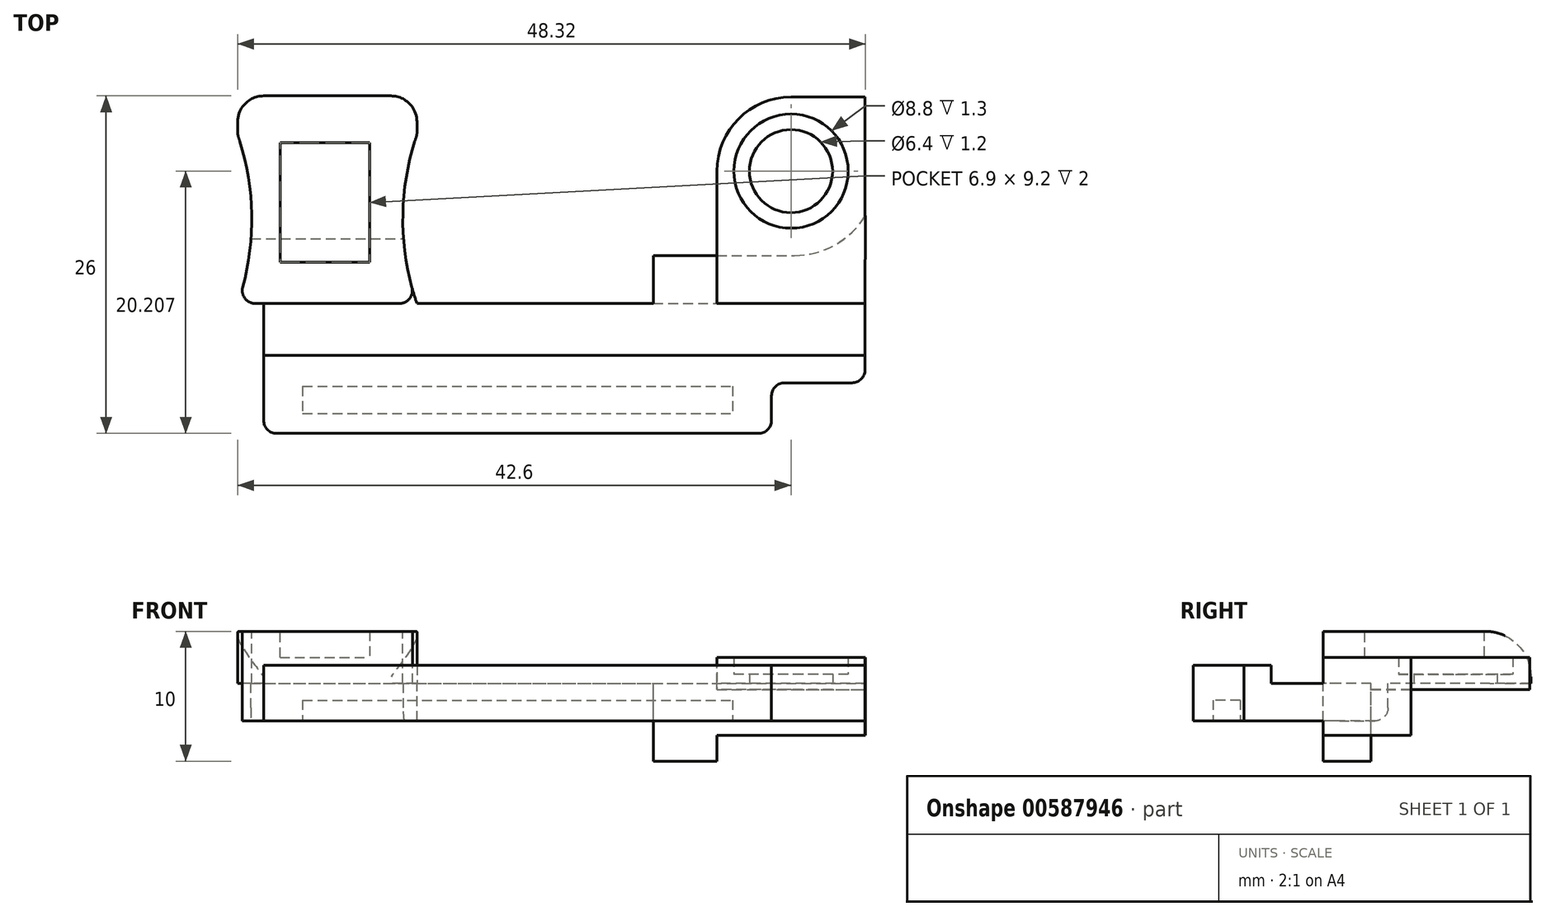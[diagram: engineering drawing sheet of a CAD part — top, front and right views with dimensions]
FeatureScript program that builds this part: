
annotation { "Feature Type Name" : "Feature", "Feature Type Description" : "" }
export const myFeature = defineFeature(function(context is Context, id is Id, definition is map)
    precondition{}
    {
        {
            var Q0;
            Q0=qCreatedBy(makeId("Top.planeOp"),FACE);
            var sketch = newSketch(context, id + "F0", { "sketchPlane" : qUnion([Q0])});
            skLineSegment(sketch, "E0.bottom", {"start": v(32.3, 6) * mm, "end": v(78.6, 6) * mm});
            skLineSegment(sketch, "E0.top", {"start": v(32.3, 0) * mm, "end": v(71.4, 0) * mm});
            skLineSegment(sketch, "E0.left", {"start": v(32.3, 6) * mm, "end": v(32.3, 0) * mm});
            skLineSegment(sketch, "E0.right", {"start": v(78.6, 6) * mm, "end": v(78.6, 3.9) * mm});
            skLineSegment(sketch, "E1.right", {"start": v(71.4, 0) * mm, "end": v(71.4, 3.9) * mm});
            skFitSpline(sketch, "E2", {"points": [v(32.3, 6) * mm, v(78.6, 6) * mm], "startDerivative": vector(78.6, 0) * mm, "endDerivative": vector(78.6, 0) * mm});
            skLineSegment(sketch, "E3", {"start": v(71.4, 3.9) * mm, "end": v(78.6, 3.9) * mm});
            skPoint(sketch, "E4.orphan", {"position": v(78.6, 0) * mm});
            skSolve(sketch);
        }
        {
            var Q0;
            {var subQ3=sQuery(id+"F0.wireOp",EDGE,"E0.left");Q0=makeQuery(id+"F0.imprint","IMPRINT",FACE,{"disambiguationData":[TD([[makeQuery(id+"F0.imprint","IMPRINT",EDGE,{"derivedFrom":subQ3}),1.0]])]});}
            extrude(context, id + "F1", {"entities" : qUnion([Q0]), "depth" : 1.4 * mm, "offsetDistance" : 25 * mm});
        }
        {
            var Q0;
            Q0=qCreatedBy(makeId("Top.planeOp"),FACE);
            var sketch = newSketch(context, id + "F2", { "sketchPlane" : qUnion([Q0])});
            skLineSegment(sketch, "E5.left", {"start": v(32.3, 6) * mm, "end": v(32.3, 0) * mm});
            skLineSegment(sketch, "E6.top", {"start": v(30.3, 10) * mm, "end": v(78.6, 10) * mm});
            skLineSegment(sketch, "E6.right", {"start": v(78.6, 3.9) * mm, "end": v(78.6, 10) * mm});
            skLineSegment(sketch, "E7.0.0", {"start": v(71.4, 0) * mm, "end": v(71.4, 3.9) * mm});
            skLineSegment(sketch, "E7.0.1", {"start": v(71.4, 3.9) * mm, "end": v(78.6, 3.9) * mm});
            skLineSegment(sketch, "E7.0.2", {"start": v(78.6, 3.9) * mm, "end": v(78.6, 6) * mm});
            skFitSpline(sketch, "E7.0.3", {"points": [v(78.6, 6) * mm, v(52.4, 6) * mm, v(58.5, 6) * mm, v(32.3, 6) * mm]});
            skLineSegment(sketch, "E7.0.5", {"start": v(32.3, 0) * mm, "end": v(71.4, 0) * mm});
            skFitSpline(sketch, "E8.0.3", {"points": [v(78.6, 6) * mm, v(52.4, 6) * mm, v(58.5, 6) * mm, v(32.3, 6) * mm]});
            skLineSegment(sketch, "E9.bottom", {"start": v(32.3, 6) * mm, "end": v(44.8, 6) * mm});
            skLineSegment(sketch, "E9.left", {"start": v(32.3, 6) * mm, "end": v(32.3, 10) * mm});
            skLineSegment(sketch, "E10.top", {"start": v(30.3, 26) * mm, "end": v(44.1, 26) * mm});
            skLineSegment(sketch, "E11.top", {"start": v(62.3, 10) * mm, "end": v(67.2, 10) * mm});
            skLineSegment(sketch, "E12", {"start": v(30.3, 23) * mm, "end": v(44.1, 23) * mm});
            skArc(sketch, "E13", {"start": v(44.1, 23) * mm, "mid": v(43.01, 16.5) * mm, "end": v(44.1, 10) * mm});
            skArc(sketch, "E14", {"start": v(30.3, 10) * mm, "mid": v(31.39, 16.5) * mm, "end": v(30.3, 23) * mm});
            skLineSegment(sketch, "E15", {"start": v(30.3, 23) * mm, "end": v(30.3, 26) * mm});
            skLineSegment(sketch, "E16", {"start": v(44.1, 26) * mm, "end": v(44.1, 23) * mm});
            skLineSegment(sketch, "E17", {"start": v(31.33, 15) * mm, "end": v(43.07, 15) * mm});
            skLineSegment(sketch, "E18.bottom", {"start": v(33.56, 22.4) * mm, "end": v(40.46, 22.4) * mm});
            skLineSegment(sketch, "E18.top", {"start": v(33.56, 13.2) * mm, "end": v(40.46, 13.2) * mm});
            skLineSegment(sketch, "E18.left", {"start": v(33.56, 22.4) * mm, "end": v(33.56, 13.2) * mm});
            skLineSegment(sketch, "E18.right", {"start": v(40.46, 22.4) * mm, "end": v(40.46, 13.2) * mm});
            skSolve(sketch);
        }
        {
            var Q0;
            Q0=qSketchRegion(id+"F2",true);
            extrude(context, id + "F3", {"entities" : qUnion([Q0]), "operationType" : NewBodyOperationType.ADD, "depth" : -1.3 * mm, "offsetDistance" : 25 * mm});
        }
        {
            var Q0;
            Q0=makeQuery(id+"F3.opExtrude","CAP_FACE",FACE,{"disambiguationData":[OSD([sQuery(id+"F2.wireOp",EDGE,"E5.top"),sQuery(id+"F2.wireOp",EDGE,"E5.left"),sQuery(id+"F2.wireOp",EDGE,"5b88ce56-a1e4-4bce-b827-63f2074a3e12.right"),sQuery(id+"F2.wireOp",EDGE,"0dff7666-cae7-412e-93f6-8a1818be1eec"),sQuery(id+"F2.wireOp",EDGE,"E6.top"),sQuery(id+"F2.wireOp",EDGE,"E6.right")])],"isStart":false});
            extrude(context, id + "F4", {"entities" : qUnion([Q0]), "operationType" : NewBodyOperationType.ADD, "depth" : 1.6 * mm, "offsetDistance" : 25 * mm});
        }
        {
            var Q0;
            Q0=makeQuery(id+"F4.opExtrude","CAP_FACE",FACE,{"disambiguationData":[OSD([sQuery(id+"F2.wireOp",EDGE,"E5.top"),sQuery(id+"F2.wireOp",EDGE,"E5.left"),sQuery(id+"F2.wireOp",EDGE,"5b88ce56-a1e4-4bce-b827-63f2074a3e12.right"),sQuery(id+"F2.wireOp",EDGE,"0dff7666-cae7-412e-93f6-8a1818be1eec"),sQuery(id+"F2.wireOp",EDGE,"E6.top"),sQuery(id+"F2.wireOp",EDGE,"E6.right")])],"isStart":false});
            var sketch = newSketch(context, id + "F5", { "sketchPlane" : qUnion([Q0])});
            skLineSegment(sketch, "E19.bottom", {"start": v(35.3, -3.63) * mm, "end": v(68.4, -3.63) * mm});
            skLineSegment(sketch, "E19.top", {"start": v(35.3, -1.53) * mm, "end": v(68.4, -1.53) * mm});
            skLineSegment(sketch, "E19.left", {"start": v(35.3, -3.63) * mm, "end": v(35.3, -1.53) * mm});
            skLineSegment(sketch, "E19.right", {"start": v(68.4, -3.63) * mm, "end": v(68.4, -1.53) * mm});
            skSolve(sketch);
        }
        {
            var Q0;
            Q0=qCreatedBy(makeId("Top.planeOp"),FACE);
            var sketch = newSketch(context, id + "F6", { "sketchPlane" : qUnion([Q0])});
            skLineSegment(sketch, "E20", {"start": v(78.62, 16.78) * mm, "end": v(78.6, 10) * mm});
            skLineSegment(sketch, "E21.0", {"start": v(67.2, 13.7) * mm, "end": v(67.2, 10) * mm});
            skLineSegment(sketch, "E22", {"start": v(78.6, 10) * mm, "end": v(67.2, 10) * mm});
            skLineSegment(sketch, "E23", {"start": v(67.2, 13.7) * mm, "end": v(73.17, 13.7) * mm});
            skArc(sketch, "E24", {"start": v(73.17, 13.7) * mm, "mid": v(76.3, 14.53) * mm, "end": v(78.62, 16.78) * mm});
            skSolve(sketch);
        }
        {
            var Q0;
            Q0=qSketchRegion(id+"F6",true);
            extrude(context, id + "F7", {"entities" : qUnion([Q0]), "oppositeDirection" : true, "depth" : 4 * mm, "offsetDistance" : 25 * mm});
        }
        {
            var Q0;
            Q0=qCreatedBy(makeId("Top.planeOp"),FACE);
            var sketch = newSketch(context, id + "F8", { "sketchPlane" : qUnion([Q0])});
            skLineSegment(sketch, "E25.bottom", {"start": v(72.9, 25.9) * mm, "end": v(78.6, 25.9) * mm});
            skLineSegment(sketch, "E25.left", {"start": v(67.2, 20.2) * mm, "end": v(67.2, 10) * mm});
            skLineSegment(sketch, "E25.right", {"start": v(78.6, 25.9) * mm, "end": v(78.6, 10) * mm});
            skCircle(sketch, "E26", {"center": v(72.9, 20.2) * mm, "radius": 3.2 * mm});
            skPoint(sketch, "E27.visualSharp", {"position": v(67.2, 25.9) * mm});
            skArc(sketch, "E27.filletArc", {"start": v(72.9, 25.9) * mm, "mid": v(68.87, 24.24) * mm, "end": v(67.2, 20.2) * mm});
            skCircle(sketch, "E28.0", {"center": v(72.9, 20.2) * mm, "radius": 4.4 * mm});
            skLineSegment(sketch, "E29", {"start": v(67.2, 10) * mm, "end": v(78.6, 10) * mm});
            skLineSegment(sketch, "E30.0", {"start": v(32.3, 0) * mm, "end": v(71.4, 0) * mm});
            skLineSegment(sketch, "E30.1", {"start": v(32.3, 6) * mm, "end": v(32.3, 0) * mm});
            skLineSegment(sketch, "E30.2", {"start": v(71.4, 3.9) * mm, "end": v(71.4, 0) * mm});
            skLineSegment(sketch, "E30.3", {"start": v(71.4, 3.9) * mm, "end": v(78.6, 3.9) * mm});
            skLineSegment(sketch, "E30.5", {"start": v(78.6, 3.9) * mm, "end": v(78.6, 10) * mm});
            skLineSegment(sketch, "E30.6", {"start": v(71.4, 0) * mm, "end": v(71.4, 3.9) * mm});
            skLineSegment(sketch, "E30.7", {"start": v(71.4, 3.9) * mm, "end": v(78.6, 3.9) * mm});
            skLineSegment(sketch, "E30.8", {"start": v(78.6, 3.9) * mm, "end": v(78.6, 6) * mm});
            skFitSpline(sketch, "E30.9", {"points": [v(78.6, 6) * mm, v(52.4, 6) * mm, v(58.5, 6) * mm, v(32.3, 6) * mm]});
            skLineSegment(sketch, "E30.10", {"start": v(32.3, 6) * mm, "end": v(32.3, 0) * mm});
            skLineSegment(sketch, "E30.13", {"start": v(71.4, 3.9) * mm, "end": v(78.6, 3.9) * mm});
            skLineSegment(sketch, "E30.14", {"start": v(78.6, 3.9) * mm, "end": v(78.6, 6) * mm});
            skFitSpline(sketch, "E30.15", {"points": [v(78.6, 6) * mm, v(52.4, 6) * mm, v(58.5, 6) * mm, v(32.3, 6) * mm]});
            skLineSegment(sketch, "E30.16", {"start": v(32.3, 6) * mm, "end": v(32.3, 0) * mm});
            skLineSegment(sketch, "E30.17", {"start": v(32.3, 0) * mm, "end": v(71.4, 0) * mm});
            skArc(sketch, "E30.18", {"start": v(73.17, 13.7) * mm, "mid": v(76.3, 14.53) * mm, "end": v(78.62, 16.78) * mm});
            skLineSegment(sketch, "E31.0", {"start": v(67.2, 13.7) * mm, "end": v(73.17, 13.7) * mm});
            skSolve(sketch);
        }
        {
            var Q0;
            Q0=makeQuery(id+"F8.imprint","IMPRINT",FACE,{"disambiguationData":[TD([[makeQuery(id+"F8.imprint","IMPRINT",EDGE,{"derivedFrom":sQuery(id+"F8.wireOp",EDGE,"E25.bottom")}),-1.0]])]});
            var Q1;
            Q1=makeQuery(id+"F6.imprint","IMPRINT",FACE,{"disambiguationData":[TD([[makeQuery(id+"F6.imprint","IMPRINT",EDGE,{"derivedFrom":sQuery(id+"F6.wireOp",EDGE,"E20")}),-1.0]])]});
            extrude(context, id + "F9", {"entities" : qUnion([Q0, Q1]), "operationType" : NewBodyOperationType.ADD, "depth" : 2 * mm, "offsetDistance" : 25 * mm});
        }
        {
            var Q0;
            Q0=makeQuery(id+"F8.imprint","IMPRINT",FACE,{"disambiguationData":[TD([[makeQuery(id+"F8.imprint","IMPRINT",EDGE,{"derivedFrom":sQuery(id+"F8.wireOp",EDGE,"E26")}),-1.0]])]});
            extrude(context, id + "F10", {"entities" : qUnion([Q0]), "operationType" : NewBodyOperationType.ADD, "depth" : 0.7 * mm, "offsetDistance" : 25 * mm});
        }
        {
            var Q0;
            {var subQ1=sQuery(id+"F8.wireOp",EDGE,"E25.bottom");Q0=makeQuery(id+"F8.imprint","IMPRINT",FACE,{"disambiguationData":[TD([[makeQuery(id+"F8.imprint","IMPRINT",EDGE,{"derivedFrom":subQ1}),-1.0]])]});}
            var Q1;
            Q1=makeQuery(id+"F8.imprint","IMPRINT",FACE,{"disambiguationData":[TD([[makeQuery(id+"F8.imprint","IMPRINT",EDGE,{"derivedFrom":sQuery(id+"F8.wireOp",EDGE,"E26")}),-1.0]])]});
            extrude(context, id + "F11", {"entities" : qUnion([Q0, Q1]), "operationType" : NewBodyOperationType.ADD, "oppositeDirection" : true, "depth" : 0.5 * mm, "offsetDistance" : 25 * mm});
        }
        {
            var Q0;
            {var subQ0=sQuery(id+"F2.wireOp",EDGE,"E6.right");Q0=makeQuery(id+"F2.imprint","IMPRINT",FACE,{"disambiguationData":[TD([[makeQuery(id+"F2.imprint","IMPRINT",EDGE,{"derivedFrom":subQ0}),1.0]])]});}
            var sketch = newSketch(context, id + "F12", { "sketchPlane" : qUnion([Q0])});
            skLineSegment(sketch, "E32.bottom", {"start": v(62.3, 13.7) * mm, "end": v(67.2, 13.7) * mm});
            skLineSegment(sketch, "E32.left", {"start": v(62.3, 13.7) * mm, "end": v(62.3, 10) * mm});
            skLineSegment(sketch, "E32.right", {"start": v(67.2, 13.7) * mm, "end": v(67.2, 10) * mm});
            skSolve(sketch);
        }
        {
            var Q0;
            Q0=makeQuery(id+"F12.imprint","IMPRINT",FACE,{"disambiguationData":[TD([[makeQuery(id+"F12.imprint","IMPRINT",EDGE,{"derivedFrom":sQuery(id+"F12.wireOp",EDGE,"E32.bottom")}),-1.0]])]});
            extrude(context, id + "F13", {"entities" : qUnion([Q0]), "operationType" : NewBodyOperationType.ADD, "oppositeDirection" : true, "depth" : 6 * mm, "offsetDistance" : 25 * mm});
        }
        {
            var Q0;
            {var subQ0=sQuery(id+"F2.wireOp",EDGE,"E12");Q0=makeQuery(id+"F2.imprint","IMPRINT",FACE,{"disambiguationData":[TD([[makeQuery(id+"F2.imprint","IMPRINT",EDGE,{"derivedFrom":subQ0}),-1.0]])]});}
            var Q1;
            Q1=makeQuery(id+"F2.imprint","IMPRINT",FACE,{"disambiguationData":[TD([[makeQuery(id+"F2.imprint","IMPRINT",EDGE,{"derivedFrom":sQuery(id+"F2.wireOp",EDGE,"E10.top")}),-1.0]])]});
            extrude(context, id + "F14", {"entities" : qUnion([Q0, Q1]), "operationType" : NewBodyOperationType.REMOVE, "endBound" : BoundingType.UP_TO_NEXT, "oppositeDirection" : true, "depth" : 25 * mm, "offsetDistance" : 25 * mm});
        }
        {
            var Q0;
            {var subQ5=sQuery(id+"F2.wireOp",EDGE,"E17");Q0=makeQuery(id+"F2.imprint","IMPRINT",FACE,{"disambiguationData":[TD([[makeQuery(id+"F2.imprint","IMPRINT",EDGE,{"derivedFrom":subQ5}),-1.0]])]});}
            var Q1;
            {var subQ0=sQuery(id+"F2.wireOp",EDGE,"E12");Q1=makeQuery(id+"F2.imprint","IMPRINT",FACE,{"disambiguationData":[TD([[makeQuery(id+"F2.imprint","IMPRINT",EDGE,{"derivedFrom":subQ0}),-1.0]])]});}
            var Q2;
            Q2=makeQuery(id+"F2.imprint","IMPRINT",FACE,{"disambiguationData":[TD([[makeQuery(id+"F2.imprint","IMPRINT",EDGE,{"derivedFrom":sQuery(id+"F2.wireOp",EDGE,"E10.top")}),-1.0]])]});
            extrude(context, id + "F15", {"entities" : qUnion([Q0, Q1, Q2]), "operationType" : NewBodyOperationType.ADD, "depth" : 4 * mm, "offsetDistance" : 25 * mm});
        }
        {
            var Q0;
            {var subQ5=sQuery(id+"F2.wireOp",EDGE,"E18.bottom");Q0=makeQuery(id+"F2.imprint","IMPRINT",FACE,{"disambiguationData":[TD([[makeQuery(id+"F2.imprint","IMPRINT",EDGE,{"derivedFrom":subQ5}),-1.0]])]});}
            var Q1;
            {var subQ5=sQuery(id+"F2.wireOp",EDGE,"E18.top");Q1=makeQuery(id+"F2.imprint","IMPRINT",FACE,{"disambiguationData":[TD([[makeQuery(id+"F2.imprint","IMPRINT",EDGE,{"derivedFrom":subQ5}),1.0]])]});}
            extrude(context, id + "F16", {"entities" : qUnion([Q0, Q1]), "operationType" : NewBodyOperationType.ADD, "depth" : 2 * mm, "offsetDistance" : 25 * mm});
        }
        {
            var Q0;
            {var subQ5=sQuery(id+"F2.wireOp",EDGE,"E18.top");Q0=makeQuery(id+"F2.imprint","IMPRINT",FACE,{"disambiguationData":[TD([[makeQuery(id+"F2.imprint","IMPRINT",EDGE,{"derivedFrom":subQ5}),1.0]])]});}
            var Q1;
            Q1=makeQuery(id+"F4.opExtrude","CAP_FACE",FACE,{"disambiguationData":[OSD([sQuery(id+"F2.wireOp",EDGE,"E6.top"),sQuery(id+"F2.wireOp",EDGE,"E6.right"),sQuery(id+"F2.wireOp",EDGE,"E7.0.0"),sQuery(id+"F2.wireOp",EDGE,"E7.0.1"),sQuery(id+"F2.wireOp",EDGE,"E7.0.2"),sQuery(id+"F2.wireOp",EDGE,"E5.left"),sQuery(id+"F2.wireOp",EDGE,"E7.0.5"),sQuery(id+"F2.wireOp",EDGE,"E10.top"),sQuery(id+"F2.wireOp",EDGE,"E9.left"),sQuery(id+"F2.wireOp",EDGE,"E11.top"),sQuery(id+"F2.wireOp",EDGE,"E13"),sQuery(id+"F2.wireOp",EDGE,"E14"),sQuery(id+"F2.wireOp",EDGE,"E15"),sQuery(id+"F2.wireOp",EDGE,"E16"),sQuery(id+"F2.wireOp",EDGE,"E18.bottom"),sQuery(id+"F2.wireOp",EDGE,"E18.top"),sQuery(id+"F2.wireOp",EDGE,"E18.left"),sQuery(id+"F2.wireOp",EDGE,"E18.right")])],"isStart":false});
            extrude(context, id + "F17", {"entities" : qUnion([Q0]), "operationType" : NewBodyOperationType.ADD, "endBound" : BoundingType.UP_TO_SURFACE, "oppositeDirection" : true, "depth" : 25 * mm, "endBoundEntityFace" : qUnion([Q1]), "offsetDistance" : 25 * mm});
        }
        {
            var Q0;
            Q0=makeQuery(id+"F5.imprint","IMPRINT",FACE,{"disambiguationData":[TD([[makeQuery(id+"F5.imprint","IMPRINT",EDGE,{"derivedFrom":sQuery(id+"F5.wireOp",EDGE,"E19.bottom")}),1.0]])]});
            extrude(context, id + "F18", {"entities" : qUnion([Q0]), "operationType" : NewBodyOperationType.REMOVE, "oppositeDirection" : true, "depth" : 1.6 * mm, "offsetDistance" : 25 * mm});
        }
        {
            var Q0;
            {var subQ0=sQuery(id+"F2.wireOp",EDGE,"E7.0.5");var subQ1=sQuery(id+"F2.wireOp",EDGE,"E7.0.0");Q0=makeQuery(id+"F4.boolean.opBoolean","MERGE",EDGE,{"derivedFrom":[makeQuery(id+"F3.boolean.opBoolean","MERGE",EDGE,{"derivedFrom":[makeQuery(id+"F1.opExtrude","SWEPT_EDGE",EDGE,{"disambiguationData":[OSD([sQuery(id+"F0.wireOp",EDGE,"E0.top"),sQuery(id+"F0.wireOp",EDGE,"E1.right")])]}),makeQuery(id+"F3.opExtrude","SWEPT_EDGE",EDGE,{"disambiguationData":[OSD([subQ1,subQ0])]})]}),makeQuery(id+"F4.opExtrude","SWEPT_EDGE",EDGE,{"disambiguationData":[OSD([subQ1,subQ0])]})]});}
            var Q1;
            Q1=makeQuery(id+"F3.opExtrude","SWEPT_EDGE",EDGE,{"disambiguationData":[OSD([sQuery(id+"F2.wireOp",EDGE,"E7.0.1"),sQuery(id+"F2.wireOp",EDGE,"E7.0.2")])]});
            var Q2;
            Q2=makeQuery(id+"F1.opExtrude","SWEPT_EDGE",EDGE,{"disambiguationData":[OSD([sQuery(id+"F0.wireOp",EDGE,"E0.top"),sQuery(id+"F0.wireOp",EDGE,"E0.left")])]});
            var Q3;
            Q3=makeQuery(id+"F4.opExtrude","SWEPT_EDGE",EDGE,{"disambiguationData":[OSD([sQuery(id+"F2.wireOp",EDGE,"E5.left"),sQuery(id+"F2.wireOp",EDGE,"E7.0.5")])]});
            var Q4;
            {var subQ0=sQuery(id+"F2.wireOp",EDGE,"E14");var subQ1=sQuery(id+"F2.wireOp",EDGE,"E6.top");Q4=makeQuery(id+"F15.boolean.opBoolean","MERGE",EDGE,{"derivedFrom":[makeQuery(id+"F4.boolean.opBoolean","MERGE",EDGE,{"derivedFrom":[makeQuery(id+"F3.opExtrude","SWEPT_EDGE",EDGE,{"disambiguationData":[OSD([subQ1,subQ0])]}),makeQuery(id+"F4.opExtrude","SWEPT_EDGE",EDGE,{"disambiguationData":[OSD([subQ1,subQ0])]})]}),makeQuery(id+"F15.opExtrude","SWEPT_EDGE",EDGE,{"disambiguationData":[OSD([subQ1,subQ0])]})]});}
            var Q5;
            Q5=makeQuery(id+"F15.opExtrude","SWEPT_EDGE",EDGE,{"disambiguationData":[OSD([sQuery(id+"F2.wireOp",EDGE,"E6.top"),sQuery(id+"F2.wireOp",EDGE,"E13")])]});
            var Q6;
            Q6=makeQuery(id+"F15.opExtrude","SWEPT_EDGE",EDGE,{"disambiguationData":[OSD([sQuery(id+"F2.wireOp",EDGE,"E12"),sQuery(id+"F2.wireOp",EDGE,"E14"),sQuery(id+"F2.wireOp",EDGE,"E15")])]});
            var Q7;
            Q7=makeQuery(id+"F15.opExtrude","SWEPT_EDGE",EDGE,{"disambiguationData":[OSD([sQuery(id+"F2.wireOp",EDGE,"E12"),sQuery(id+"F2.wireOp",EDGE,"E13"),sQuery(id+"F2.wireOp",EDGE,"E16")])]});
            var Q8;
            {var subQ0=sQuery(id+"F2.wireOp",EDGE,"E17");Q8=makeQuery(id+"F17.boolean.opBoolean","MERGE",EDGE,{"derivedFrom":[makeQuery(id+"F14.boolean.opBoolean","COPY",EDGE,{"derivedFrom":makeQuery(id+"F14.opExtrude","CAP_EDGE",EDGE,{"disambiguationData":[OSD([subQ0]),TDD([makeQuery(id+"F2.imprint","IMPRINT",EDGE,{"disambiguationData":[TD([[makeQuery(id+"F2.imprint","INTERSECT",VERTEX,{"derivedFrom":[sQuery(id+"F2.wireOp",EDGE,"E14"),subQ0]}),-1.0]])],"derivedFrom":subQ0})])],"isStart":false})}),makeQuery(id+"F14.boolean.opBoolean","COPY",EDGE,{"derivedFrom":makeQuery(id+"F14.opExtrude","CAP_EDGE",EDGE,{"disambiguationData":[OSD([subQ0]),TDD([makeQuery(id+"F2.imprint","IMPRINT",EDGE,{"disambiguationData":[TD([[makeQuery(id+"F2.imprint","INTERSECT",VERTEX,{"derivedFrom":[sQuery(id+"F2.wireOp",EDGE,"E13"),subQ0]}),1.0]])],"derivedFrom":subQ0})])],"isStart":false})}),makeQuery(id+"F17.opExtrude","CAP_EDGE",EDGE,{"disambiguationData":[OSD([subQ0])],"isStart":false})]});}
            fillet(context, id + "F19", {"entities" : qUnion([Q0, Q1, Q2, Q3, Q4, Q5, Q6, Q7, Q8]), "radius" : 1 * mm, "tangentPropagation" : true, "allowEdgeOverflow" : false});
        }
        {
            var Q0;
            Q0=makeQuery(id+"F15.opExtrude","SWEPT_EDGE",EDGE,{"disambiguationData":[OSD([sQuery(id+"F2.wireOp",EDGE,"E10.top"),sQuery(id+"F2.wireOp",EDGE,"E15")])]});
            var Q1;
            Q1=makeQuery(id+"F15.opExtrude","SWEPT_EDGE",EDGE,{"disambiguationData":[OSD([sQuery(id+"F2.wireOp",EDGE,"E10.top"),sQuery(id+"F2.wireOp",EDGE,"E16")])]});
            fillet(context, id + "F20", {"entities" : qUnion([Q0, Q1]), "radius" : 2 * mm, "tangentPropagation" : true, "allowEdgeOverflow" : false});
        }
        {
            var Q0;
            Q0=makeQuery(id+"F15.opExtrude","CAP_EDGE",EDGE,{"disambiguationData":[OSD([sQuery(id+"F2.wireOp",EDGE,"E10.top")])],"isStart":false});
            fillet(context, id + "F21", {"entities" : qUnion([Q0]), "radius" : 3.5 * mm, "allowEdgeOverflow" : false});
        }
    });
